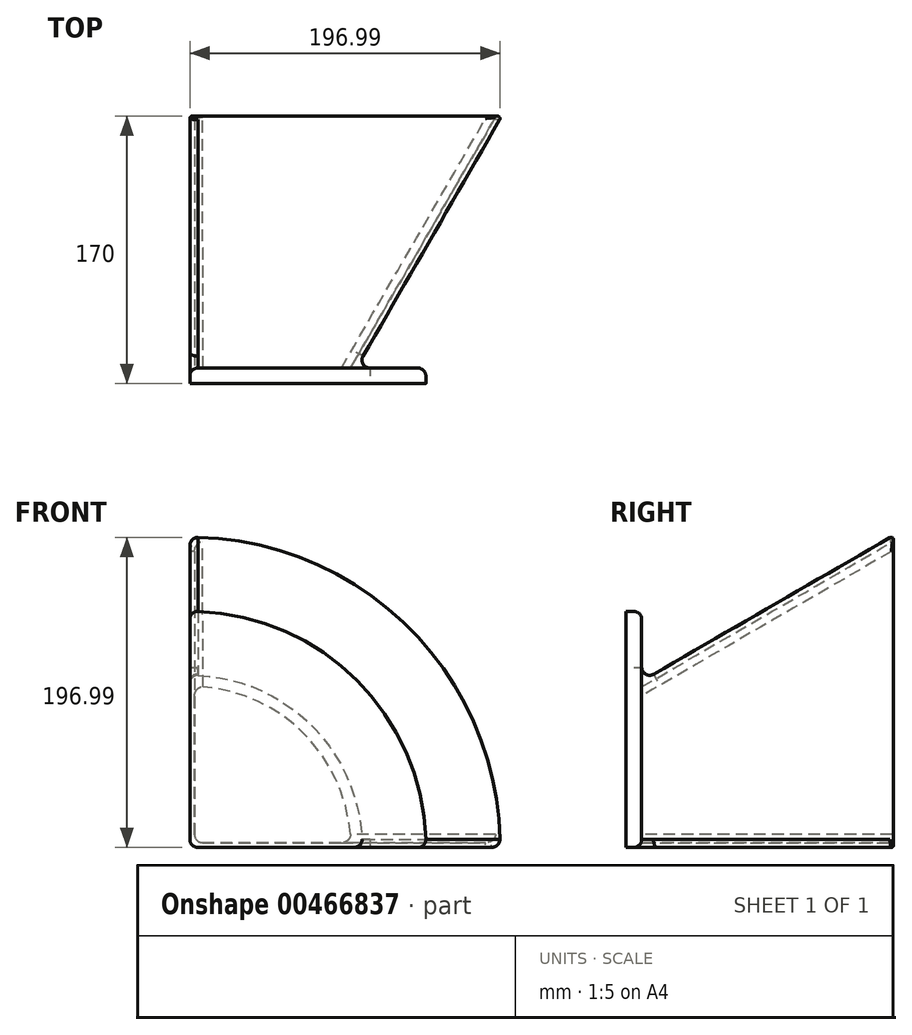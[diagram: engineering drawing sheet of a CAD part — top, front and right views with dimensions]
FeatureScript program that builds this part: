
annotation { "Feature Type Name" : "Feature", "Feature Type Description" : "" }
export const myFeature = defineFeature(function(context is Context, id is Id, definition is map)
    precondition{}
    {
        {
            var Q0;
            Q0=qCreatedBy(makeId("Top.planeOp"),FACE);
            var sketch = newSketch(context, id + "F0", { "sketchPlane" : qUnion([Q0])});
            skLineSegment(sketch, "E0", {"start": v(0, 170) * mm, "end": v(0, 0) * mm});
            skLineSegment(sketch, "E1", {"start": v(0, 0) * mm, "end": v(100, 0) * mm});
            skLineSegment(sketch, "E2", {"start": v(100, 0) * mm, "end": v(198.15, 170) * mm});
            skLineSegment(sketch, "E3", {"start": v(198.15, 170) * mm, "end": v(0, 170) * mm});
            skSolve(sketch);
        }
        {
            var Q0;
            Q0=makeQuery(id+"F0.imprint","IMPRINT",FACE,{"disambiguationData":[TD([[makeQuery(id+"F0.imprint","IMPRINT",EDGE,{"derivedFrom":sQuery(id+"F0.wireOp",EDGE,"E0")}),1.0]])]});
            var Q1;
            Q1=sQuery(id+"F0.wireOp",EDGE,"E0");
            revolve(context, id + "F1", {"entities" : qUnion([Q0]), "axis" : qUnion([Q1]), "revolveType" : RevolveType.ONE_DIRECTION, "angle" : 90 * degree});
        }
        {
            var Q0;
            Q0=makeQuery(id+"F1.opRevolve","SWEPT_FACE",FACE,{"disambiguationData":[OSD([sQuery(id+"F0.wireOp",EDGE,"E3")])]});
            shell(context, id + "F2", {"entities" : qUnion([Q0]), "thickness" : 3 * mm});
        }
        {
            var Q0;
            Q0=makeQuery(id+"F1.opRevolve","SWEPT_FACE",FACE,{"disambiguationData":[OSD([sQuery(id+"F0.wireOp",EDGE,"E1")])]});
            var sketch = newSketch(context, id + "F3", { "sketchPlane" : qUnion([Q0])});
            skArc(sketch, "E4", {"start": v(150, 0) * mm, "mid": v(106.07, 106.07) * mm, "end": v(0, 150) * mm});
            skLineSegment(sketch, "E5", {"start": v(0, 0) * mm, "end": v(0, 150) * mm});
            skLineSegment(sketch, "E6", {"start": v(0, 0) * mm, "end": v(150, 0) * mm});
            skPoint(sketch, "E6.endSnap0", {"position": v(50, 0) * mm});
            skSolve(sketch);
        }
        {
            var Q0;
            {var subQ0=sQuery(id+"F3.wireOp",EDGE,"E4");Q0=makeQuery(id+"F3.imprint","IMPRINT",FACE,{"disambiguationData":[TD([[makeQuery(id+"F3.imprint","IMPRINT",EDGE,{"derivedFrom":subQ0}),1.0]])]});}
            var Q1;
            {var subQ3=makeQuery(id+"F1.opRevolve","SWEPT_EDGE",EDGE,{"disambiguationData":[OSD([sQuery(id+"F0.wireOp",EDGE,"E1"),sQuery(id+"F0.wireOp",EDGE,"E2")])]});Q1=makeQuery(id+"F3.imprint","IMPRINT",FACE,{"disambiguationData":[TD([[makeQuery(id+"F3.imprint","IMPRINT",EDGE,{"derivedFrom":subQ3}),-1.0]])]});}
            extrude(context, id + "F4", {"entities" : qUnion([Q0, Q1]), "operationType" : NewBodyOperationType.ADD, "oppositeDirection" : true, "depth" : 10 * mm});
        }
        {
            var Q0;
            Q0=makeQuery(id+"F4.opExtrude","CAP_EDGE",EDGE,{"disambiguationData":[OSD([sQuery(id+"F3.wireOp",EDGE,"E4")])],"isStart":false});
            var Q1;
            Q1=makeQuery(id+"F4.opExtrude","CAP_EDGE",EDGE,{"disambiguationData":[OSD([sQuery(id+"F3.wireOp",EDGE,"E6")])],"isStart":false});
            var Q2;
            Q2=makeQuery(id+"F4.opExtrude","CAP_EDGE",EDGE,{"disambiguationData":[OSD([sQuery(id+"F3.wireOp",EDGE,"E5")])],"isStart":false});
            var Q3;
            Q3=makeQuery(id+"F4.opExtrude","SWEPT_EDGE",EDGE,{"disambiguationData":[OSD([sQuery(id+"F3.wireOp",EDGE,"E4"),sQuery(id+"F3.wireOp",EDGE,"E6")])]});
            var Q4;
            Q4=makeQuery(id+"F4.opExtrude","SWEPT_EDGE",EDGE,{"disambiguationData":[OSD([sQuery(id+"F3.wireOp",EDGE,"E4"),sQuery(id+"F3.wireOp",EDGE,"E5")])]});
            var Q5;
            Q5=makeQuery(id+"F4.boolean.opBoolean","INTERSECT",EDGE,{"derivedFrom":[makeQuery(id+"F1.opRevolve","SWEPT_FACE",FACE,{"disambiguationData":[OSD([sQuery(id+"F0.wireOp",EDGE,"E2")])]}),makeQuery(id+"F4.opExtrude","CAP_FACE",FACE,{"disambiguationData":[OSD([sQuery(id+"F3.wireOp",EDGE,"E4"),sQuery(id+"F3.wireOp",EDGE,"E5"),sQuery(id+"F3.wireOp",EDGE,"E6")])],"isStart":false})]});
            fillet(context, id + "F5", {"entities" : qUnion([Q0, Q1, Q2, Q3, Q4, Q5]), "radius" : 5 * mm, "tangentPropagation" : true, "allowEdgeOverflow" : false});
        }
        {
            var Q0;
            Q0=makeQuery(id+"F1.opRevolve","CAP_EDGE",EDGE,{"disambiguationData":[OSD([sQuery(id+"F0.wireOp",EDGE,"E0")])],"isStart":true});
            var Q1;
            Q1=makeQuery(id+"F2.opShell","OFFSET_EDGE",EDGE,{"disambiguationData":[OSD([sQuery(id+"F0.wireOp",EDGE,"E0")])]});
            var Q2;
            {var subQ0=sQuery(id+"F0.wireOp",EDGE,"E2");Q2=makeQuery(id+"F2.opShell","OFFSET_EDGE",EDGE,{"disambiguationData":[OSD([subQ0]),TDD([makeQuery(id+"F1.opRevolve","CAP_EDGE",EDGE,{"disambiguationData":[OSD([subQ0])],"isStart":false})])]});}
            var Q3;
            {var subQ0=sQuery(id+"F0.wireOp",EDGE,"E2");Q3=makeQuery(id+"F2.opShell","OFFSET_EDGE",EDGE,{"disambiguationData":[OSD([subQ0]),TDD([makeQuery(id+"F1.opRevolve","CAP_EDGE",EDGE,{"disambiguationData":[OSD([subQ0])],"isStart":true})])]});}
            var Q4;
            Q4=makeQuery(id+"F1.opRevolve","CAP_EDGE",EDGE,{"disambiguationData":[OSD([sQuery(id+"F0.wireOp",EDGE,"E2")])],"isStart":false});
            var Q5;
            Q5=makeQuery(id+"F1.opRevolve","CAP_EDGE",EDGE,{"disambiguationData":[OSD([sQuery(id+"F0.wireOp",EDGE,"E2")])],"isStart":true});
            fillet(context, id + "F6", {"entities" : qUnion([Q0, Q1, Q2, Q3, Q4, Q5]), "radius" : 5 * mm, "tangentPropagation" : true, "allowEdgeOverflow" : false});
        }
        {
            var Q0;
            Q0=makeQuery(id+"F1.opRevolve","SWEPT_EDGE",EDGE,{"disambiguationData":[OSD([sQuery(id+"F0.wireOp",EDGE,"E2"),sQuery(id+"F0.wireOp",EDGE,"E3")])]});
            var Q1;
            Q1=makeQuery(id+"F2.opShell","OFFSET_EDGE",EDGE,{"disambiguationData":[OSD([sQuery(id+"F0.wireOp",EDGE,"E2"),sQuery(id+"F0.wireOp",EDGE,"E3")])]});
            fillet(context, id + "F7", {"entities" : qUnion([Q0, Q1]), "radius" : 1.5 * mm, "tangentPropagation" : true, "allowEdgeOverflow" : false});
        }
    });
